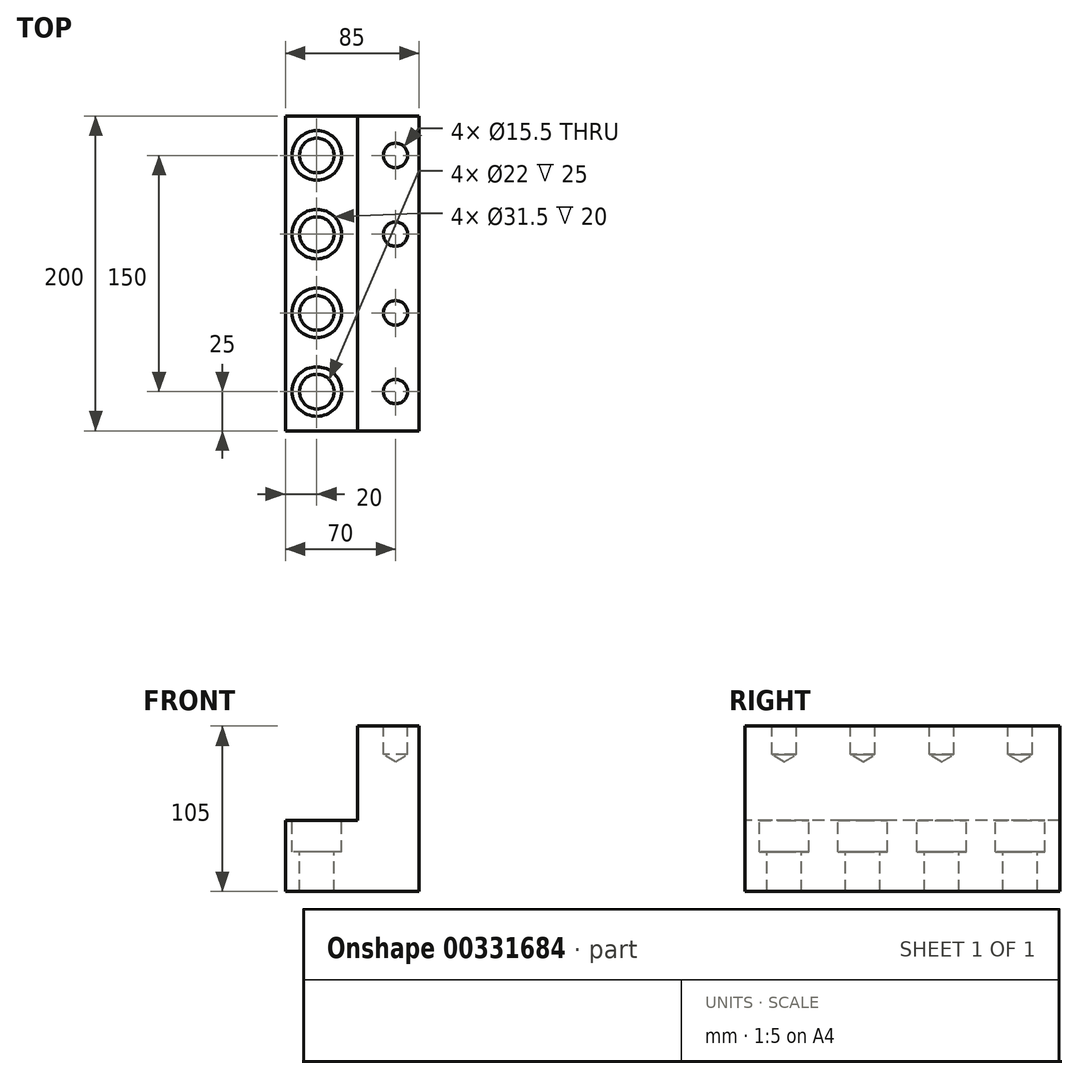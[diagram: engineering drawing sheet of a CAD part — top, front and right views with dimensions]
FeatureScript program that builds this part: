
annotation { "Feature Type Name" : "Feature", "Feature Type Description" : "" }
export const myFeature = defineFeature(function(context is Context, id is Id, definition is map)
    precondition{}
    {
        {
            var Q0;
            Q0=qCreatedBy(makeId("Front.planeOp"),FACE);
            var sketch = newSketch(context, id + "F0", { "sketchPlane" : qUnion([Q0])});
            skLineSegment(sketch, "E0.bottom", {"start": v(-46, 45) * mm, "end": v(39, 45) * mm});
            skLineSegment(sketch, "E0.top", {"start": v(-46, 0) * mm, "end": v(39, 0) * mm});
            skLineSegment(sketch, "E0.left", {"start": v(-46, 45) * mm, "end": v(-46, 0) * mm});
            skLineSegment(sketch, "E0.right", {"start": v(39, 45) * mm, "end": v(39, 0) * mm});
            skLineSegment(sketch, "E1.bottom", {"start": v(0, 105) * mm, "end": v(39, 105) * mm});
            skLineSegment(sketch, "E1.top", {"start": v(0, 45) * mm, "end": v(39, 45) * mm});
            skLineSegment(sketch, "E1.left", {"start": v(0, 105) * mm, "end": v(0, 45) * mm});
            skLineSegment(sketch, "E1.right", {"start": v(39, 105) * mm, "end": v(39, 45) * mm});
            skSolve(sketch);
        }
        {
            var Q0;
            Q0=makeQuery(id+"F0.imprint","IMPRINT",FACE,{"disambiguationData":[TD([[makeQuery(id+"F0.imprint","IMPRINT",EDGE,{"derivedFrom":sQuery(id+"F0.wireOp",EDGE,"E1.bottom")}),-1.0]])]});
            var Q1;
            Q1=makeQuery(id+"F0.imprint","IMPRINT",FACE,{"disambiguationData":[TD([[makeQuery(id+"F0.imprint","IMPRINT",EDGE,{"derivedFrom":sQuery(id+"F0.wireOp",EDGE,"E0.bottom")}),-1.0]])]});
            extrude(context, id + "F1", {"entities" : qUnion([Q0, Q1]), "oppositeDirection" : true, "depth" : 200 * mm});
        }
        {
            var Q0;
            Q0=makeQuery(id+"F1.opExtrude","SWEPT_FACE",FACE,{"disambiguationData":[OSD([sQuery(id+"F0.wireOp",EDGE,"E0.bottom")])]});
            var sketch = newSketch(context, id + "F2", { "sketchPlane" : qUnion([Q0])});
            skCircle(sketch, "E2", {"center": v(-26, 25) * mm, "radius": 10 * mm});
            skCircle(sketch, "E3", {"center": v(-26, 25) * mm, "radius": 15 * mm});
            skCircle(sketch, "E4.0.1.0", {"center": v(-26, 75) * mm, "radius": 10 * mm});
            skCircle(sketch, "E4.0.1.1", {"center": v(-26, 75) * mm, "radius": 15 * mm});
            skCircle(sketch, "E4.0.2.0", {"center": v(-26, 125) * mm, "radius": 10 * mm});
            skCircle(sketch, "E4.0.2.1", {"center": v(-26, 125) * mm, "radius": 15 * mm});
            skCircle(sketch, "E4.0.3.0", {"center": v(-26, 175) * mm, "radius": 10 * mm});
            skCircle(sketch, "E4.0.3.1", {"center": v(-26, 175) * mm, "radius": 15 * mm});
            skLineSegment(sketch, "E4.direction1", {"start": v(-26, 25) * mm, "end": v(11.53, 25) * mm, "construction": true});
            skLineSegment(sketch, "E4.direction2", {"start": v(-26, 25) * mm, "end": v(-26, 75) * mm, "construction": true});
            skSolve(sketch);
        }
        {
            var Q0;
            Q0=makeQuery(id+"F1.opExtrude","SWEPT_FACE",FACE,{"disambiguationData":[OSD([sQuery(id+"F0.wireOp",EDGE,"E1.bottom")])]});
            var sketch = newSketch(context, id + "F3", { "sketchPlane" : qUnion([Q0])});
            skCircle(sketch, "E5", {"center": v(24, 25) * mm, "radius": 7 * mm});
            skCircle(sketch, "E6.0.1.0", {"center": v(24, 75) * mm, "radius": 7 * mm});
            skCircle(sketch, "E6.0.2.0", {"center": v(24, 125) * mm, "radius": 7 * mm});
            skCircle(sketch, "E6.0.3.0", {"center": v(24, 175) * mm, "radius": 7 * mm});
            skLineSegment(sketch, "E6.direction1", {"start": v(24, 25) * mm, "end": v(49, 25) * mm, "construction": true});
            skLineSegment(sketch, "E6.direction2", {"start": v(24, 25) * mm, "end": v(24, 75) * mm, "construction": true});
            skSolve(sketch);
        }
        {
            var Q0;
            Q0=sQuery(id+"F3.wireOp",VERTEX,"TgFbm2Ur-gzMK-JnJ2-a0Jp-dKqBmY9SFvuD.center");
            var Q1;
            Q1=sQuery(id+"F3.wireOp",VERTEX,"E5.center");
            var Q2;
            Q2=sQuery(id+"F3.wireOp",VERTEX,"E6.0.1.0.center");
            var Q3;
            Q3=sQuery(id+"F3.wireOp",VERTEX,"E6.0.2.0.center");
            var Q4;
            Q4=sQuery(id+"F3.wireOp",VERTEX,"E6.0.3.0.center");
            var Q5;
            Q5=makeQuery(id+"F1.opExtrude","SWEPT_BODY",BODY,{"disambiguationData":[OSD([sQuery(id+"F0.wireOp",EDGE,"E0.bottom"),sQuery(id+"F0.wireOp",EDGE,"E0.top"),sQuery(id+"F0.wireOp",EDGE,"E0.left"),sQuery(id+"F0.wireOp",EDGE,"E0.right"),sQuery(id+"F0.wireOp",EDGE,"E1.bottom"),sQuery(id+"F0.wireOp",EDGE,"E1.left"),sQuery(id+"F0.wireOp",EDGE,"E1.right")])]});
            hole(context, id + "F4", {"style" : HoleStyle.SIMPLE, "endStyle" : HoleEndStyle.BLIND, "standardTappedOrClearance" : lookupTablePath({ "standard" : "ISO", "fit" : "Normal", "size" : "M14", "type" : "Clearance" }), "standardBlindInLast" : lookupTablePath({ "fit" : "Standard", "standard" : "ISO", "size" : "M14", "type" : "Clearance" }), "holeDiameter" : 15.5 * mm, "holeDepth" : 18 * mm, "tappedDepth" : 12 * mm, "tapClearance" : 3, "locations" : qUnion([Q0, Q1, Q2, Q3, Q4]), "scope" : qUnion([Q5])});
        }
        {
            var Q0;
            Q0=sQuery(id+"F2.wireOp",VERTEX,"ecfc04b5-88dd-4b3f-8d35-bfd3a53baa78.center");
            var Q1;
            Q1=sQuery(id+"F2.wireOp",VERTEX,"E2.center");
            var Q2;
            Q2=sQuery(id+"F2.wireOp",VERTEX,"E4.0.1.1.center");
            var Q3;
            Q3=sQuery(id+"F2.wireOp",VERTEX,"E4.0.2.0.center");
            var Q4;
            Q4=sQuery(id+"F2.wireOp",VERTEX,"E4.0.3.0.center");
            var Q5;
            Q5=makeQuery(id+"F1.opExtrude","SWEPT_BODY",BODY,{"disambiguationData":[OSD([sQuery(id+"F0.wireOp",EDGE,"E0.bottom"),sQuery(id+"F0.wireOp",EDGE,"E0.top"),sQuery(id+"F0.wireOp",EDGE,"E0.left"),sQuery(id+"F0.wireOp",EDGE,"E0.right"),sQuery(id+"F0.wireOp",EDGE,"E1.bottom"),sQuery(id+"F0.wireOp",EDGE,"E1.left"),sQuery(id+"F0.wireOp",EDGE,"E1.right")])]});
            hole(context, id + "F5", {"style" : HoleStyle.C_BORE, "endStyle" : HoleEndStyle.THROUGH, "standardTappedOrClearance" : lookupTablePath({ "standard" : "ISO", "fit" : "Normal", "size" : "M20", "type" : "Clearance" }), "standardBlindInLast" : lookupTablePath({ "fit" : "Standard", "standard" : "ISO", "size" : "M20", "type" : "Clearance" }), "holeDiameter" : 22 * mm, "cBoreDiameter" : 31.5 * mm, "cBoreDepth" : 20 * mm, "tappedDepth" : 12 * mm, "tapClearance" : 3, "locations" : qUnion([Q0, Q1, Q2, Q3, Q4]), "scope" : qUnion([Q5])});
        }
    });
